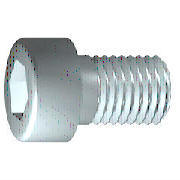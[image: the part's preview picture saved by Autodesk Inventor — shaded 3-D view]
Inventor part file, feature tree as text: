
AUTODESK INVENTOR PART (.ipt)
format: ipt  version: 2018 (Build 220112000, 112)  size: 192,000 bytes
history: native  units: mm (DEFAULTED — no unit token found)
features: sketch x2, extrude x1, plane x1, fillet x1
ambient origin geometry x7: Origin, YZ Plane, XY Plane, X Axis, Y Axis, Z Axis, Center Point
bodies: Solid1 (feature_tree), Body (feature_tree)
feature tree (5):
  extrude  "Slot"  Depth=5.0mm
  plane  "Work Plane1"
  fillet  "Fillet2"  Radius=5.0mm
  sketch  "Sketch1"  dims[d1=13.90924mm d2=0.49086mm d3=5.0mm]
  sketch  "Sketch2"  dims[d4=2.5mm d5=60.0deg d6=5.0mm d7=5.0mm d8=4.618802mm d9=8.5mm d10=90.0deg d11=10.0mm d12=0.0mm d13=13.90924mm d14=0.0mm d15=0.49076mm d16=0.49076mm d17=0.5mm d19=0.0mm d26=16.0mm d27=45.0deg d28=0.0mm d29=0.0mm d30=0.1mm]
